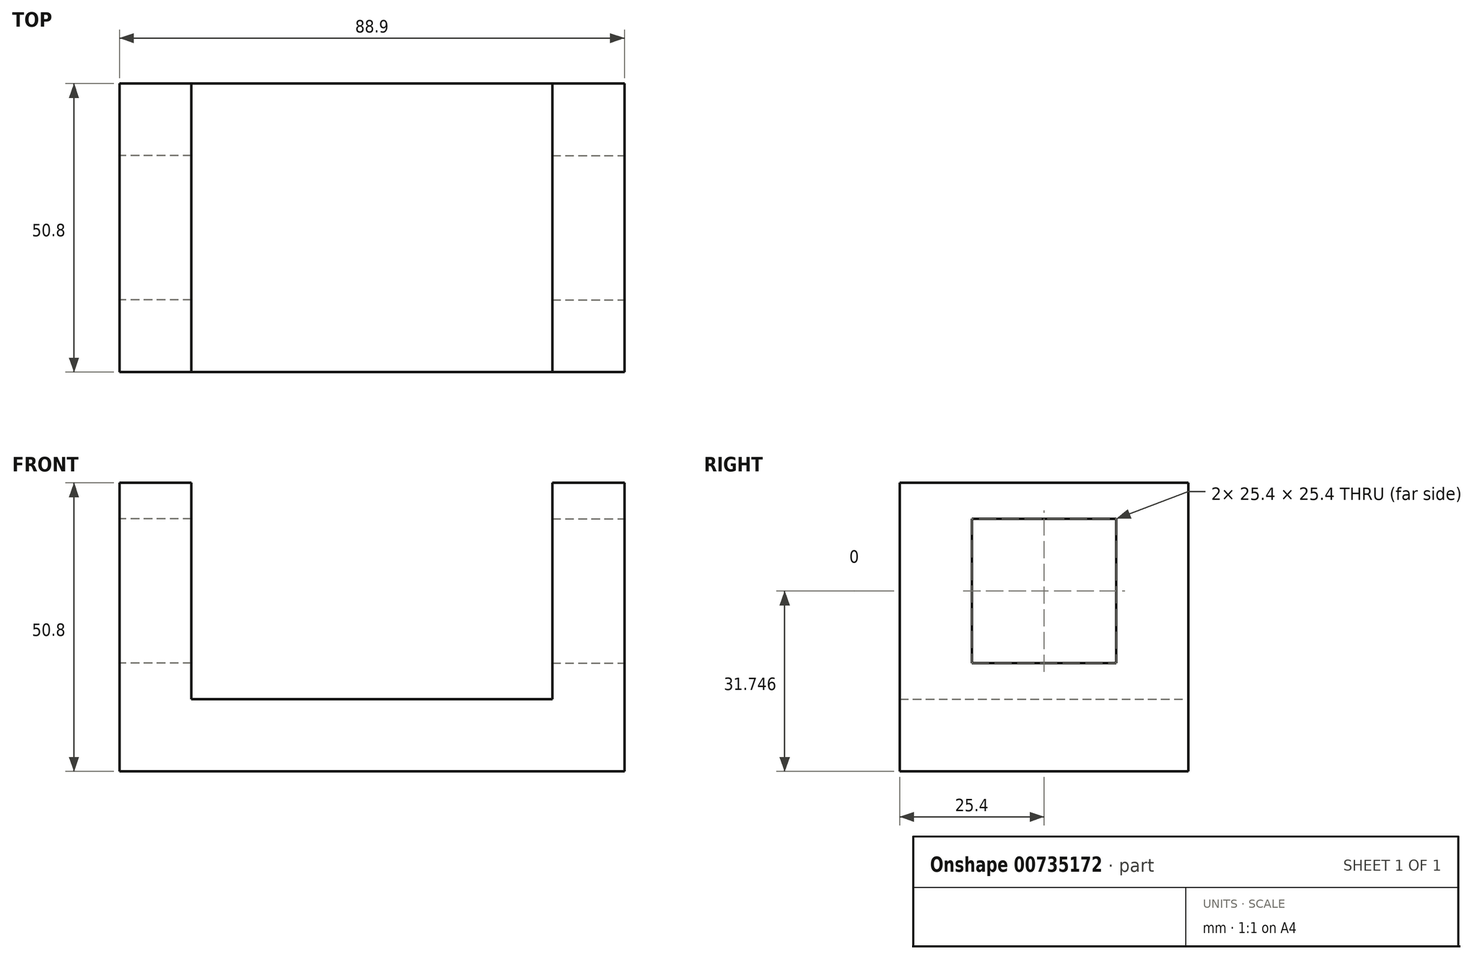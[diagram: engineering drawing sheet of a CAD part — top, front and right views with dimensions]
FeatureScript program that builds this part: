
annotation { "Feature Type Name" : "Feature", "Feature Type Description" : "" }
export const myFeature = defineFeature(function(context is Context, id is Id, definition is map)
    precondition{}
    {
        {
            var Q0;
            Q0=qCreatedBy(makeId("Front.planeOp"),FACE);
            var sketch = newSketch(context, id + "F0", { "sketchPlane" : qUnion([Q0])});
            skLineSegment(sketch, "E0", {"start": v(0, 23) * mm, "end": v(12.7, 23) * mm});
            skLineSegment(sketch, "E1", {"start": v(12.7, 23) * mm, "end": v(12.7, -15.1) * mm});
            skLineSegment(sketch, "E2", {"start": v(0, 23) * mm, "end": v(0, -27.8) * mm});
            skLineSegment(sketch, "E3", {"start": v(0, -27.8) * mm, "end": v(88.9, -27.8) * mm});
            skLineSegment(sketch, "E4", {"start": v(12.7, -15.1) * mm, "end": v(76.2, -15.1) * mm});
            skLineSegment(sketch, "E5", {"start": v(76.2, -15.1) * mm, "end": v(76.2, 23) * mm});
            skLineSegment(sketch, "E6", {"start": v(76.2, 23) * mm, "end": v(88.9, 23) * mm});
            skLineSegment(sketch, "E7", {"start": v(88.9, 23) * mm, "end": v(88.9, -27.8) * mm});
            skSolve(sketch);
        }
        {
            var Q0;
            Q0=makeQuery(id+"F0.imprint","IMPRINT",FACE,{"disambiguationData":[TD([[makeQuery(id+"F0.imprint","IMPRINT",EDGE,{"derivedFrom":sQuery(id+"F0.wireOp",EDGE,"E0")}),-1.0]])]});
            extrude(context, id + "F1", {"entities" : qUnion([Q0]), "depth" : 50.8 * mm, "offsetDistance" : 25.4 * mm});
        }
        {
            var Q0;
            Q0=makeQuery(id+"F1.opExtrude","SWEPT_FACE",FACE,{"disambiguationData":[OSD([sQuery(id+"F0.wireOp",EDGE,"E7")])]});
            var sketch = newSketch(context, id + "F2", { "sketchPlane" : qUnion([Q0])});
            skLineSegment(sketch, "E8", {"start": v(-38.1, 16.66) * mm, "end": v(-12.7, 16.66) * mm});
            skLineSegment(sketch, "E9", {"start": v(-12.7, 16.66) * mm, "end": v(-12.7, -8.74) * mm});
            skLineSegment(sketch, "E10", {"start": v(-12.7, -8.74) * mm, "end": v(-38.1, -8.74) * mm});
            skLineSegment(sketch, "E11", {"start": v(-38.1, -8.74) * mm, "end": v(-38.1, 16.66) * mm});
            skLineSegment(sketch, "E12", {"start": v(-21.28, -8.74) * mm, "end": v(-21.28, -27.8) * mm});
            skLineSegment(sketch, "E13", {"start": v(-12.7, 3.96) * mm, "end": v(0, 3.96) * mm});
            skSolve(sketch);
        }
        {
            var Q0;
            {var subQ5=sQuery(id+"F2.wireOp",EDGE,"E8");Q0=makeQuery(id+"F2.imprint","IMPRINT",FACE,{"disambiguationData":[TD([[makeQuery(id+"F2.imprint","IMPRINT",EDGE,{"derivedFrom":subQ5}),-1.0]])]});}
            extrude(context, id + "F3", {"entities" : qUnion([Q0]), "operationType" : NewBodyOperationType.REMOVE, "oppositeDirection" : true, "depth" : 12.7 * mm, "offsetDistance" : 25.4 * mm});
        }
        {
            var Q0;
            Q0=makeQuery(id+"F1.opExtrude","SWEPT_FACE",FACE,{"disambiguationData":[OSD([sQuery(id+"F0.wireOp",EDGE,"E2")])]});
            var sketch = newSketch(context, id + "F4", { "sketchPlane" : qUnion([Q0])});
            skLineSegment(sketch, "E14", {"start": v(12.7, 16.66) * mm, "end": v(38.1, 16.66) * mm});
            skLineSegment(sketch, "E15", {"start": v(38.1, 16.66) * mm, "end": v(38.1, -8.74) * mm});
            skLineSegment(sketch, "E16", {"start": v(38.1, -8.74) * mm, "end": v(12.7, -8.74) * mm});
            skLineSegment(sketch, "E17", {"start": v(12.7, 16.66) * mm, "end": v(12.7, -8.74) * mm});
            skLineSegment(sketch, "E18", {"start": v(27.33, -8.74) * mm, "end": v(27.33, -27.8) * mm});
            skLineSegment(sketch, "E19", {"start": v(38.1, 3.96) * mm, "end": v(50.8, 3.96) * mm});
            skLineSegment(sketch, "E20", {"start": v(21.05, -8.74) * mm, "end": v(21.05, -27.8) * mm});
            skSolve(sketch);
        }
        {
            var Q0;
            {var subQ5=sQuery(id+"F4.wireOp",EDGE,"E14");Q0=makeQuery(id+"F4.imprint","IMPRINT",FACE,{"disambiguationData":[TD([[makeQuery(id+"F4.imprint","IMPRINT",EDGE,{"derivedFrom":subQ5}),-1.0]])]});}
            extrude(context, id + "F5", {"entities" : qUnion([Q0]), "operationType" : NewBodyOperationType.REMOVE, "oppositeDirection" : true, "depth" : 12.7 * mm, "offsetDistance" : 25.4 * mm});
        }
    });
